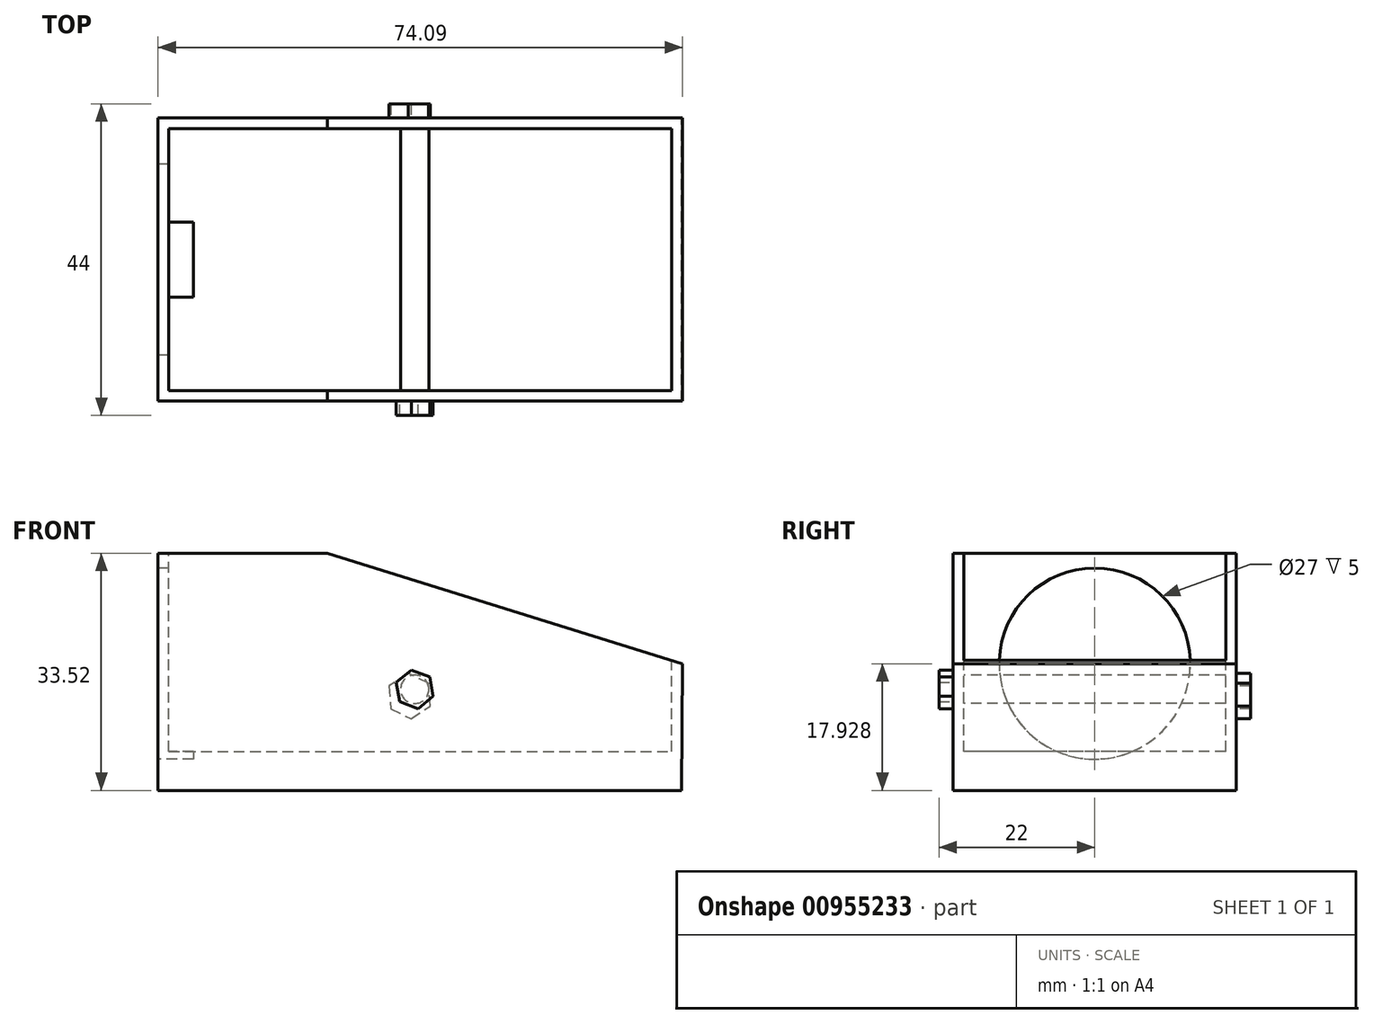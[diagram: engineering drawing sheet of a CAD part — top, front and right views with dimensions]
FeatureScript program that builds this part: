
annotation { "Feature Type Name" : "Feature", "Feature Type Description" : "" }
export const myFeature = defineFeature(function(context is Context, id is Id, definition is map)
    precondition{}
    {
        {
            var Q0;
            Q0=qCreatedBy(makeId("Front.planeOp"),FACE);
            var sketch = newSketch(context, id + "F0", { "sketchPlane" : qUnion([Q0])});
            skLineSegment(sketch, "E0.bottom", {"start": v(-23.91, 0) * mm, "end": v(50.03, 0) * mm});
            skLineSegment(sketch, "E0.left", {"start": v(-23.91, 0) * mm, "end": v(-23.91, 33.52) * mm});
            skLineSegment(sketch, "E1", {"start": v(-23.91, 33.52) * mm, "end": v(0, 33.52) * mm});
            skLineSegment(sketch, "E2", {"start": v(0, 33.52) * mm, "end": v(50.18, 17.91) * mm});
            skLineSegment(sketch, "E3", {"start": v(50.18, 17.91) * mm, "end": v(50.03, 0) * mm});
            skSolve(sketch);
        }
        {
            var Q0;
            Q0=makeQuery(id+"F0.imprint","IMPRINT",FACE,{"disambiguationData":[TD([[makeQuery(id+"F0.imprint","IMPRINT",EDGE,{"derivedFrom":sQuery(id+"F0.wireOp",EDGE,"E0.bottom")}),1.0]])]});
            extrude(context, id + "F1", {"entities" : qUnion([Q0]), "depth" : 20 * mm, "offsetDistance" : 25 * mm});
        }
        {
            var Q0;
            Q0=makeQuery(id+"F1.opExtrude","SWEPT_BODY",BODY,{"disambiguationData":[OSD([sQuery(id+"F0.wireOp",EDGE,"E0.bottom"),sQuery(id+"F0.wireOp",EDGE,"E0.top"),sQuery(id+"F0.wireOp",EDGE,"E0.left"),sQuery(id+"F0.wireOp",EDGE,"E0.right")])]});
            var Q1;
            Q1=makeQuery(id+"F1.opExtrude","CAP_FACE",FACE,{"disambiguationData":[OSD([sQuery(id+"F0.wireOp",EDGE,"E0.bottom"),sQuery(id+"F0.wireOp",EDGE,"E0.top"),sQuery(id+"F0.wireOp",EDGE,"E0.left"),sQuery(id+"F0.wireOp",EDGE,"E0.right")])],"isStart":true});
            mirror(context, id + "F2", {"operationType" : NewBodyOperationType.ADD, "entities" : qUnion([Q0]), "mirrorPlane" : qUnion([Q1])});
        }
        {
            var Q0;
            {var subQ0=makeQuery(id+"F1.opExtrude","SWEPT_FACE",FACE,{"disambiguationData":[OSD([sQuery(id+"F0.wireOp",EDGE,"E1")])]});Q0=makeQuery(id+"F2.boolean.opBoolean","MERGE",FACE,{"derivedFrom":[subQ0,makeQuery(id+"F2.opPattern","COPY",FACE,{"derivedFrom":subQ0,"instanceName":"1"})]});}
            var sketch = newSketch(context, id + "F3", { "sketchPlane" : qUnion([Q0])});
            skLineSegment(sketch, "E4.bottom", {"start": v(-22.41, 18.5) * mm, "end": v(48.68, 18.5) * mm});
            skLineSegment(sketch, "E4.top", {"start": v(-22.41, -18.5) * mm, "end": v(48.68, -18.5) * mm});
            skLineSegment(sketch, "E4.left", {"start": v(-22.41, 18.5) * mm, "end": v(-22.41, -18.5) * mm});
            skLineSegment(sketch, "E4.right", {"start": v(48.68, 18.5) * mm, "end": v(48.68, -18.5) * mm});
            skSolve(sketch);
        }
        {
            var Q0;
            Q0=makeQuery(id+"F3.imprint","IMPRINT",FACE,{"disambiguationData":[TD([[makeQuery(id+"F3.imprint","IMPRINT",EDGE,{"derivedFrom":sQuery(id+"F3.wireOp",EDGE,"E4.bottom")}),-1.0]])]});
            extrude(context, id + "F4", {"entities" : qUnion([Q0]), "operationType" : NewBodyOperationType.REMOVE, "oppositeDirection" : true, "depth" : 28 * mm, "offsetDistance" : 25 * mm});
        }
        {
            var Q0;
            Q0=makeQuery(id+"F1.opExtrude","CAP_FACE",FACE,{"disambiguationData":[OSD([sQuery(id+"F0.wireOp",EDGE,"E0.bottom"),sQuery(id+"F0.wireOp",EDGE,"E0.left"),sQuery(id+"F0.wireOp",EDGE,"E1"),sQuery(id+"F0.wireOp",EDGE,"E2"),sQuery(id+"F0.wireOp",EDGE,"E3")])],"isStart":false});
            var sketch = newSketch(context, id + "F5", { "sketchPlane" : qUnion([Q0])});
            skCircle(sketch, "E5", {"center": v(12.35, 14.3) * mm, "radius": 2 * mm});
            skCircle(sketch, "E6.cCircle", {"center": v(12.35, 14.3) * mm, "radius": 2.4 * mm, "construction": true});
            skLineSegment(sketch, "E6.0", {"start": v(14.48, 16.08) * mm, "end": v(14.95, 13.35) * mm});
            skLineSegment(sketch, "E6.1", {"start": v(14.95, 13.35) * mm, "end": v(12.82, 11.58) * mm});
            skLineSegment(sketch, "E6.2", {"start": v(12.82, 11.58) * mm, "end": v(10.22, 12.53) * mm});
            skLineSegment(sketch, "E6.3", {"start": v(10.22, 12.53) * mm, "end": v(9.75, 15.27) * mm});
            skLineSegment(sketch, "E6.4", {"start": v(9.75, 15.27) * mm, "end": v(11.88, 17.04) * mm});
            skLineSegment(sketch, "E6.5", {"start": v(11.88, 17.04) * mm, "end": v(14.48, 16.08) * mm});
            skPoint(sketch, "E6.0.midPoint", {"position": v(14.72, 14.72) * mm});
            skSolve(sketch);
        }
        {
            var Q0;
            Q0=makeQuery(id+"F5.imprint","IMPRINT",FACE,{"disambiguationData":[TD([[makeQuery(id+"F5.imprint","IMPRINT",EDGE,{"derivedFrom":sQuery(id+"F5.wireOp",EDGE,"E5")}),-1.0]])]});
            extrude(context, id + "F6", {"entities" : qUnion([Q0]), "operationType" : NewBodyOperationType.ADD, "depth" : 2 * mm, "offsetDistance" : 25 * mm});
        }
        {
            var Q0;
            Q0=makeQuery(id+"F6.boolean.opBoolean","SPLIT",FACE,{"disambiguationData":[TD([makeQuery(id+"F6.opExtrude","SWEPT_FACE",FACE,{"disambiguationData":[OSD([sQuery(id+"F5.wireOp",EDGE,"E5")])]})])],"derivedFrom":makeQuery(id+"F1.opExtrude","CAP_FACE",FACE,{"disambiguationData":[OSD([sQuery(id+"F0.wireOp",EDGE,"E0.bottom"),sQuery(id+"F0.wireOp",EDGE,"E0.left"),sQuery(id+"F0.wireOp",EDGE,"E1"),sQuery(id+"F0.wireOp",EDGE,"E2"),sQuery(id+"F0.wireOp",EDGE,"E3")])],"isStart":false})});
            extrude(context, id + "F7", {"entities" : qUnion([Q0]), "operationType" : NewBodyOperationType.ADD, "oppositeDirection" : true, "depth" : 40 * mm, "offsetDistance" : 25 * mm});
        }
        {
            var Q0;
            Q0=makeQuery(id+"F6.boolean.opBoolean","SPLIT",FACE,{"disambiguationData":[TD([makeQuery(id+"F6.opExtrude","SWEPT_FACE",FACE,{"disambiguationData":[OSD([sQuery(id+"F5.wireOp",EDGE,"E5")])]})])],"derivedFrom":makeQuery(id+"F1.opExtrude","CAP_FACE",FACE,{"disambiguationData":[OSD([sQuery(id+"F0.wireOp",EDGE,"E0.bottom"),sQuery(id+"F0.wireOp",EDGE,"E0.left"),sQuery(id+"F0.wireOp",EDGE,"E1"),sQuery(id+"F0.wireOp",EDGE,"E2"),sQuery(id+"F0.wireOp",EDGE,"E3")])],"isStart":false})});
            extrude(context, id + "F8", {"entities" : qUnion([Q0]), "operationType" : NewBodyOperationType.ADD, "depth" : 2 * mm, "offsetDistance" : 25 * mm});
        }
        {
            var Q0;
            Q0=makeQuery(id+"F2.opPattern","COPY",FACE,{"derivedFrom":makeQuery(id+"F1.opExtrude","CAP_FACE",FACE,{"disambiguationData":[OSD([sQuery(id+"F0.wireOp",EDGE,"E0.bottom"),sQuery(id+"F0.wireOp",EDGE,"E0.left"),sQuery(id+"F0.wireOp",EDGE,"E1"),sQuery(id+"F0.wireOp",EDGE,"E2"),sQuery(id+"F0.wireOp",EDGE,"E3")])],"isStart":false}),"instanceName":"1"});
            var sketch = newSketch(context, id + "F9", { "sketchPlane" : qUnion([Q0])});
            skCircle(sketch, "E7.cCircle", {"center": v(-11.63, 13.35) * mm, "radius": 2.8 * mm, "construction": true});
            skLineSegment(sketch, "E7.0", {"start": v(-8.74, 14.78) * mm, "end": v(-8.95, 11.55) * mm});
            skLineSegment(sketch, "E7.1", {"start": v(-8.95, 11.55) * mm, "end": v(-11.85, 10.13) * mm});
            skLineSegment(sketch, "E7.2", {"start": v(-11.85, 10.13) * mm, "end": v(-14.53, 11.92) * mm});
            skLineSegment(sketch, "E7.3", {"start": v(-14.53, 11.92) * mm, "end": v(-14.32, 15.14) * mm});
            skLineSegment(sketch, "E7.4", {"start": v(-14.32, 15.14) * mm, "end": v(-11.42, 16.57) * mm});
            skLineSegment(sketch, "E7.5", {"start": v(-11.42, 16.57) * mm, "end": v(-8.74, 14.78) * mm});
            skPoint(sketch, "E7.0.midPoint", {"position": v(-8.85, 13.17) * mm});
            skSolve(sketch);
        }
        {
            var Q0;
            Q0=makeQuery(id+"F9.imprint","IMPRINT",FACE,{"disambiguationData":[TD([[makeQuery(id+"F9.imprint","IMPRINT",EDGE,{"derivedFrom":sQuery(id+"F9.wireOp",EDGE,"E7.0")}),-1.0]])]});
            extrude(context, id + "F10", {"entities" : qUnion([Q0]), "operationType" : NewBodyOperationType.ADD, "depth" : 2 * mm, "offsetDistance" : 25 * mm});
        }
        {
            var Q0;
            {var subQ0=makeQuery(id+"F1.opExtrude","SWEPT_FACE",FACE,{"disambiguationData":[OSD([sQuery(id+"F0.wireOp",EDGE,"E0.left")])]});Q0=makeQuery(id+"F2.boolean.opBoolean","MERGE",FACE,{"derivedFrom":[subQ0,makeQuery(id+"F2.opPattern","COPY",FACE,{"derivedFrom":subQ0,"instanceName":"1"})]});}
            var sketch = newSketch(context, id + "F11", { "sketchPlane" : qUnion([Q0])});
            skCircle(sketch, "E8", {"center": v(0, 17.93) * mm, "radius": 13.5 * mm});
            skSolve(sketch);
        }
        {
            var Q0;
            Q0=makeQuery(id+"F11.imprint","IMPRINT",FACE,{"disambiguationData":[TD([[makeQuery(id+"F11.imprint","IMPRINT",EDGE,{"derivedFrom":sQuery(id+"F11.wireOp",EDGE,"E8")}),1.0]])]});
            extrude(context, id + "F12", {"entities" : qUnion([Q0]), "operationType" : NewBodyOperationType.REMOVE, "oppositeDirection" : true, "depth" : 5 * mm, "offsetDistance" : 25 * mm});
        }
    });
